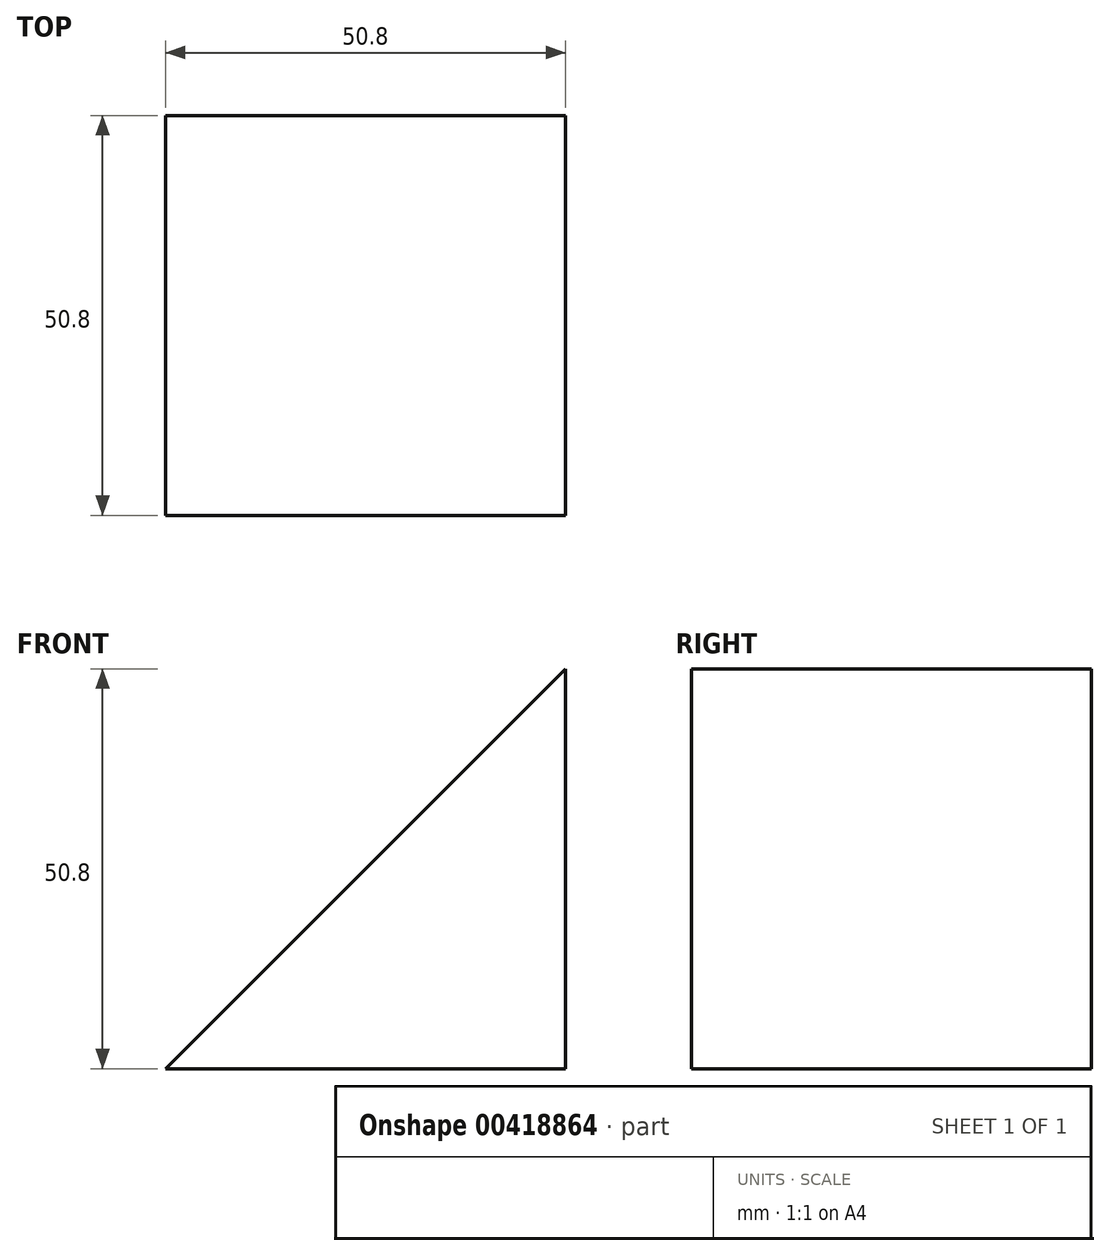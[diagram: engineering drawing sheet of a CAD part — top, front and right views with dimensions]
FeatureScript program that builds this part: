
annotation { "Feature Type Name" : "Feature", "Feature Type Description" : "" }
export const myFeature = defineFeature(function(context is Context, id is Id, definition is map)
    precondition{}
    {
        {
            var Q0;
            Q0=qCreatedBy(makeId("Front.planeOp"),FACE);
            var sketch = newSketch(context, id + "F0", { "sketchPlane" : qUnion([Q0])});
            skLineSegment(sketch, "E0", {"start": v(0, 0) * mm, "end": v(0, 50.8) * mm});
            skLineSegment(sketch, "E1", {"start": v(0, 0) * mm, "end": v(-50.8, 0) * mm});
            skLineSegment(sketch, "E2", {"start": v(0, 50.8) * mm, "end": v(-50.8, 0) * mm});
            skSolve(sketch);
        }
        {
            var Q0;
            Q0 = qSketchRegion(id + "F0", true);
            extrude(context, id + "F1", {"entities" : qUnion([Q0]), "depth" : 50.8 * mm});
        }
    });
